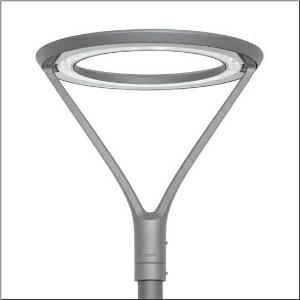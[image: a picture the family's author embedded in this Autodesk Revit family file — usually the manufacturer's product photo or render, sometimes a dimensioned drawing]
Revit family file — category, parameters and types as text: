
# Revit family: dl_r__20___p1_0a_5xa51283nr008_4ff5
name_source: partatom
category: Lighting Fixtures
units: mm (PartAtom-declared; Revit-internal decimal feet)

## family parameters
Cut with Voids When Loaded = No
Host = Face
Light Source = No
Part Type = Normal
Room Calculation Point = No
Round Connector Dimension = Use Diameter
Shared = No

## types (1)
- --- (1 x LED, 3040 lm, 23.2 W, 4000K)
    Apparent Load = 23 VA
    CIE Flux Codes = 31 71 96 100 100
    Color Rendering = 70
    Color Temperature = 4000K
    Default Elevation = 1800 mm
    Description = DL® 20, mast luminaire, primary light control with cycle path optic, highly specular, primary optical cover: cover, of toughened safety glass of clear glass with excellent transmission level, light distribution: P1.0a, light emission: direct distribution, primary light characteristic: asymmetric, installation type: post-top, LED, High Power LED, rated luminous flux: 3.050lm, luminous efficacy: 112lm/W, light colour: 740, colour temperature: 4000K, control gear: Plus, control: overheat protection, power reduction, digital communication interface, constant luminous flux control, time-dependent luminous flux control, flexible luminous flux parameterisation, electronic power reduction, mains connection: 230..240V, 50/60Hz, connection cable pre-assembled, cable length: 5m, start of lifetime: 27W, end of service life: 28W, reduction: 14W, luminaire housing, upper part, of cast aluminium, powder-coated, Siteco® metallic grey (DB 702S), diameter: 690mm, height: 690mm, spigot size: 76mm (post-top), mounting height: 4..6m, luminaire housing, of cast aluminium, powder-coated, Siteco® metallic grey (DB 702S), equipment: standard, protection rating (complete): IP66, insulation class (complete): insulation class II (safety insulation), certification: CE, ENEC, VDE, impact resistance: IK08, permissible operating ambient temperature: -25..+35°C, standard-compliant lighting for roads and squares, packaging unit: 1 piece

Light Distribution: P1.0a
    Height = 690 mm
    Lamp = 1 x LED
    Lamp Light Flux = 3040 lm
    Lamp Power = 23.2 W
    Lamp count = 1
    Length = 690 mm
    Luminous efficacy = 131 lm/W
    Manufacturer = Siteco
    ModVariant = No
    Model = 5XA51283NR008
    Number of Poles = 1
    OnlyDefault = Yes
    Power Factor = 1
    Product Name = DL® 20 | P1.0a
    Product group = mast luminaire | pylon top
    ProductGroupID = 6100
    Protection Class = Protection class II
    Protection Degree = IP 66
    RLX_Detail_Level = 1
    RLX_Emergency_Light_Flux = 0 lm
    RLX_Emergency_Type = 0
    RLX_Emergency_Type_DB = No
    RlxData = <blob elided: 206773 chars, md5=2004c682>
    Socket = socket
    Standby Power = 0 W
    System Light Flux = 3040 lm
    System Power = 23 W
    Type Comments = factory setting: luminous flux: 100 % | dim-lin: 254 | 310 mA
    Type Image = l_1006001.jpg
    URL = http://relux.com
    VarID = @adj_076676
    Voltage = 0 V
    Weight = 0.00 kg
    Width = 0 mm  [stored 0 ft]

note: [stored X ft] marks values corroborated as IEEE doubles in the binary element streams (Revit-internal decimal feet)

## geometry (parser evidence)
native form markers: Blend x4, Sweep x11
no freeform markers — native parametric forms only
